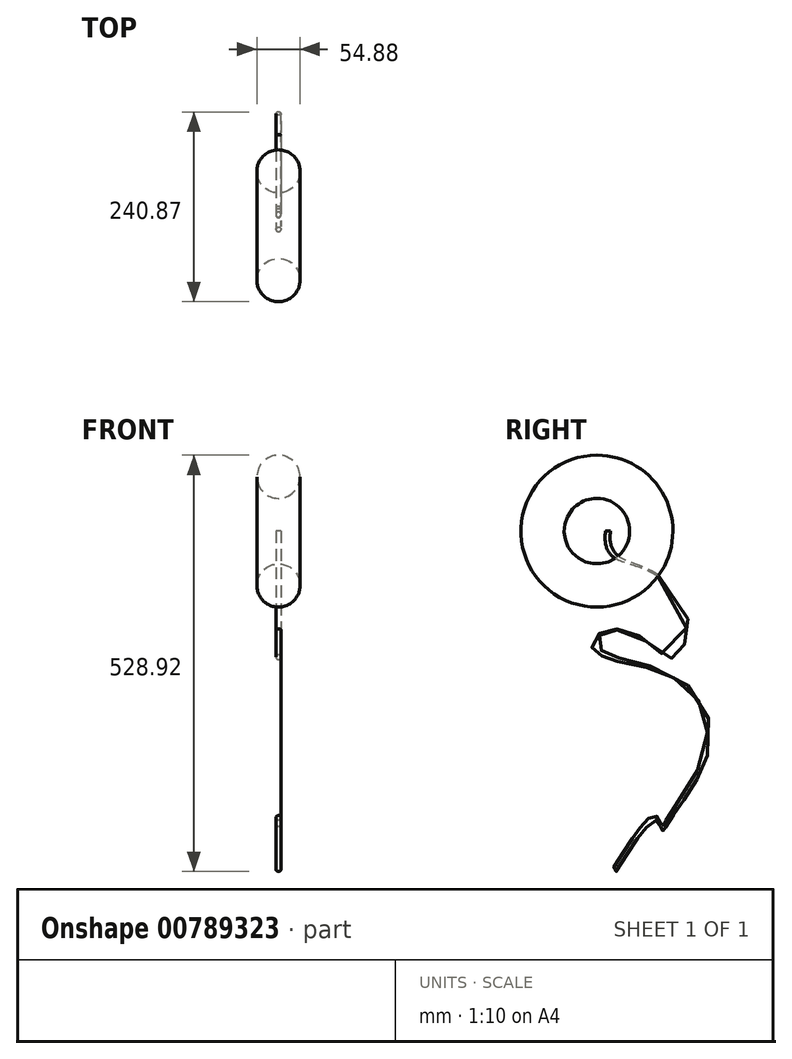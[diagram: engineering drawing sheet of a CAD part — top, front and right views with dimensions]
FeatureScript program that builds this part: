
annotation { "Feature Type Name" : "Feature", "Feature Type Description" : "" }
export const myFeature = defineFeature(function(context is Context, id is Id, definition is map)
    precondition{}
    {
        {
            var Q0;
            Q0=qCreatedBy(makeId("Front.planeOp"),FACE);
            var sketch = newSketch(context, id + "F0", { "sketchPlane" : qUnion([Q0])});
            skCircle(sketch, "E0", {"center": v(0, 69.04) * mm, "radius": 27.44 * mm});
            skLineSegment(sketch, "E1", {"start": v(-76, 0) * mm, "end": v(74.69, 0) * mm, "construction": true});
            skSolve(sketch);
        }
        {
            var Q0;
            Q0=makeQuery(id+"F0.imprint","IMPRINT",FACE,{"disambiguationData":[TD([[makeQuery(id+"F0.imprint","IMPRINT",EDGE,{"derivedFrom":sQuery(id+"F0.wireOp",EDGE,"E0")}),1.0]])]});
            var Q1;
            Q1=sQuery(id+"F0.wireOp",EDGE,"E1");
            revolve(context, id + "F1", {"surfaceOperationType" : NewSurfaceOperationType.NEW, "entities" : qUnion([Q0]), "axis" : qUnion([Q1]), "revolveType" : RevolveType.FULL});
        }
        {
            var Q0;
            Q0=qCreatedBy(makeId("Right.planeOp"),FACE);
            var sketch = newSketch(context, id + "F2", { "sketchPlane" : qUnion([Q0])});
            skFitSpline(sketch, "E2", {"points": [v(0, -76.58) * mm, v(40.96, -129.7) * mm, v(0, -170.28) * mm, v(7.7, -212.94) * mm, v(76, -266.1) * mm, v(13.2, -361.92) * mm, v(0, -372.3) * mm, v(-52.08, -450.5) * mm], "startDerivative": vector(385.03, -618.93) * mm, "endDerivative": vector(-376.73, -602.23) * mm});
            skSolve(sketch);
        }
        {
            var Q0;
            Q0=qCreatedBy(makeId("Top.planeOp"),FACE);
            var sketch = newSketch(context, id + "F3", { "sketchPlane" : qUnion([Q0])});
            skCircle(sketch, "E3", {"center": v(0, 14.22) * mm, "radius": 3.18 * mm});
            skSolve(sketch);
        }
        {
            var Q0;
            Q0=makeQuery(id+"F3.imprint","IMPRINT",FACE,{"disambiguationData":[TD([[makeQuery(id+"F3.imprint","IMPRINT",EDGE,{"derivedFrom":sQuery(id+"F3.wireOp",EDGE,"E3")}),1.0]])]});
            var Q1;
            Q1 = qSketchRegion(id + "F2", true);
            var Q2;
            Q2=sQuery(id+"F2.wireOp",EDGE,"E2");
            sweep(context, id + "F4", {"profiles" : qUnion([Q0, Q1]), "path" : qUnion([Q2])});
        }
    });
